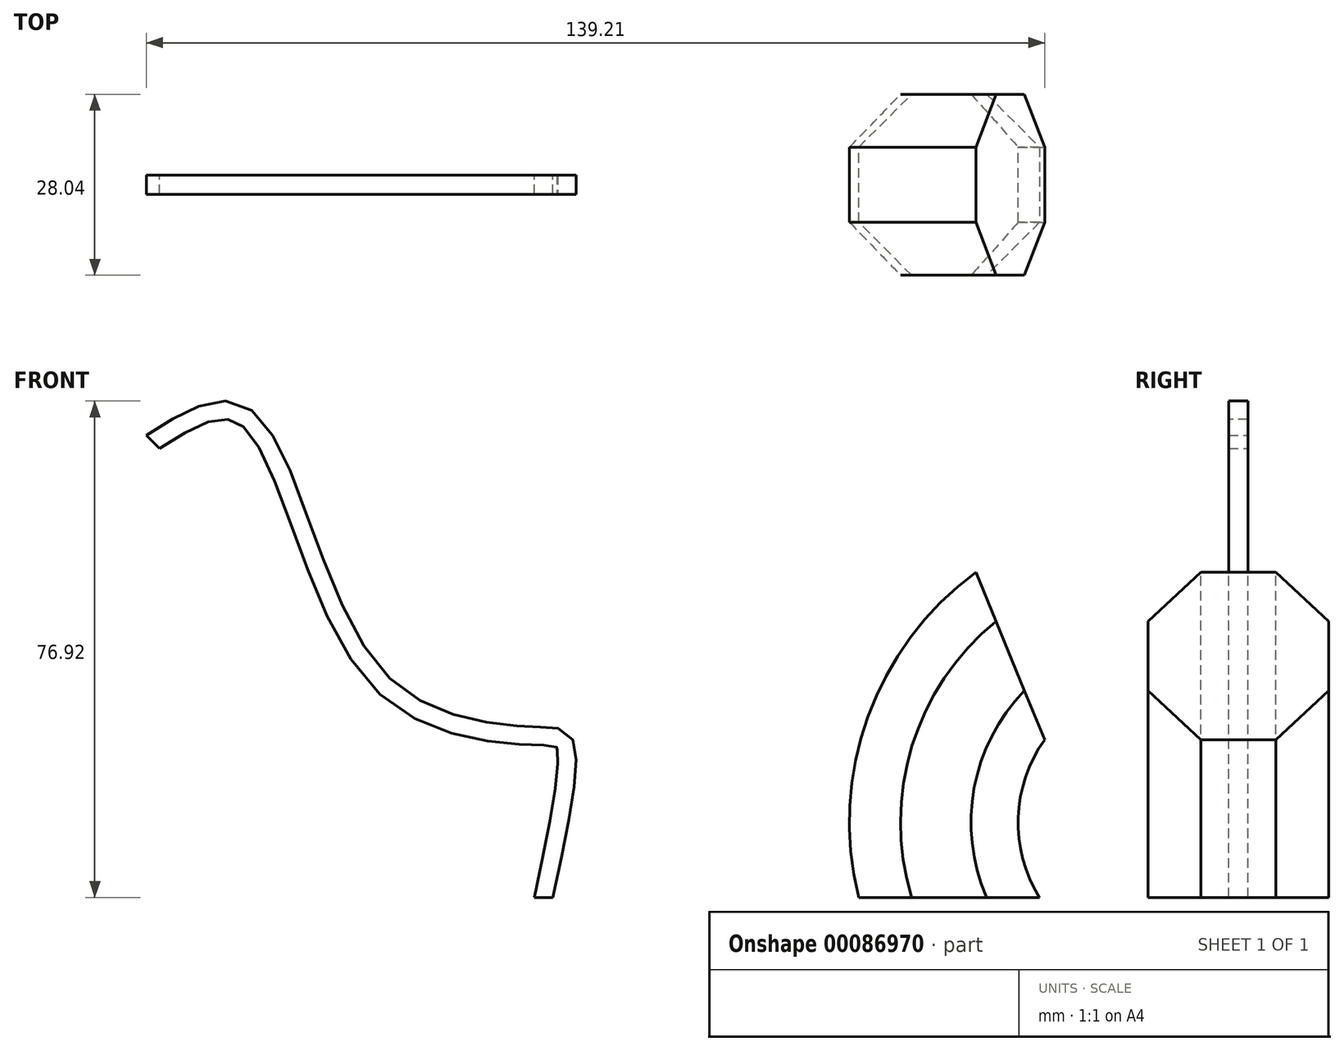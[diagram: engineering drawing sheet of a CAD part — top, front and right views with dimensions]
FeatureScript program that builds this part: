
annotation { "Feature Type Name" : "Feature", "Feature Type Description" : "" }
export const myFeature = defineFeature(function(context is Context, id is Id, definition is map)
    precondition{}
    {
        {
            var Q0;
            Q0=qCreatedBy(makeId("Front.planeOp"),FACE);
            var sketch = newSketch(context, id + "F0", { "sketchPlane" : qUnion([Q0])});
            skLineSegment(sketch, "E0", {"start": v(0, 0) * mm, "end": v(46.88, 0) * mm, "construction": true});
            skLineSegment(sketch, "E1", {"start": v(46.88, 0) * mm, "end": v(46.88, 46.88) * mm, "construction": true});
            skLineSegment(sketch, "E2", {"start": v(46.88, 46.88) * mm, "end": v(0, 0) * mm, "construction": true});
            skLineSegment(sketch, "E3", {"start": v(46.88, 0) * mm, "end": v(23.44, 23.44) * mm, "construction": true});
            skLineSegment(sketch, "E4", {"start": v(23.44, 23.44) * mm, "end": v(9.47, 37.41) * mm, "construction": true});
            skArc(sketch, "E5.trimOffspring", {"start": v(9.47, 37.41) * mm, "mid": v(-0.96, 20.15) * mm, "end": v(0, 0) * mm});
            skSolve(sketch);
        }
        {
            var Q0;
            Q0=qCreatedBy(makeId("Top.planeOp"),FACE);
            var sketch = newSketch(context, id + "F1", { "sketchPlane" : qUnion([Q0])});
            skCircle(sketch, "E6.cCircle", {"center": v(0, 0) * mm, "radius": 14.02 * mm, "construction": true});
            skLineSegment(sketch, "E6.0", {"start": v(5.8, -14.02) * mm, "end": v(-5.8, -14.02) * mm});
            skLineSegment(sketch, "E6.1", {"start": v(-5.8, -14.02) * mm, "end": v(-14.02, -5.8) * mm});
            skLineSegment(sketch, "E6.2", {"start": v(-14.02, -5.8) * mm, "end": v(-14.02, 5.8) * mm});
            skLineSegment(sketch, "E6.3", {"start": v(-14.02, 5.8) * mm, "end": v(-5.8, 14.02) * mm});
            skLineSegment(sketch, "E6.4", {"start": v(-5.8, 14.02) * mm, "end": v(5.8, 14.02) * mm});
            skLineSegment(sketch, "E6.5", {"start": v(5.8, 14.02) * mm, "end": v(14.02, 5.8) * mm});
            skLineSegment(sketch, "E6.6", {"start": v(14.02, 5.8) * mm, "end": v(14.02, -5.8) * mm});
            skLineSegment(sketch, "E6.7", {"start": v(14.02, -5.8) * mm, "end": v(5.8, -14.02) * mm});
            skPoint(sketch, "E6.0.midPoint", {"position": v(0, -14.02) * mm});
            skSolve(sketch);
        }
        {
            var Q0;
            Q0=makeQuery(id+"F1.imprint","IMPRINT",FACE,{"disambiguationData":[TD([[makeQuery(id+"F1.imprint","IMPRINT",EDGE,{"derivedFrom":sQuery(id+"F1.wireOp",EDGE,"E6.0")}),-1.0]])]});
            var Q1;
            Q1=sQuery(id+"F0.wireOp",EDGE,"E5.trimOffspring");
            sweep(context, id + "F2", {"profiles" : qUnion([Q0]), "path" : qUnion([Q1])});
        }
        {
            var Q0;
            Q0=qCreatedBy(makeId("Front.planeOp"),FACE);
            var sketch = newSketch(context, id + "F3", { "sketchPlane" : qUnion([Q0])});
            skFitSpline(sketch, "E7", {"points": [v(-62.87, 0) * mm, v(-59.54, 23.6) * mm, v(-62.68, 24.97) * mm, v(-88.14, 33.4) * mm, v(-108.9, 74.33) * mm, v(-123.4, 70.6) * mm], "startDerivative": vector(30.74, 142.34) * mm, "endDerivative": vector(-91.72, -58.96) * mm});
            skSolve(sketch);
        }
        {
            var Q0;
            Q0=qCreatedBy(makeId("Top.planeOp"),FACE);
            var sketch = newSketch(context, id + "F4", { "sketchPlane" : qUnion([Q0])});
            skLineSegment(sketch, "E8.bottom", {"start": v(-61.43, -1.5) * mm, "end": v(-64.32, -1.5) * mm});
            skLineSegment(sketch, "E8.top", {"start": v(-61.43, 1.5) * mm, "end": v(-64.32, 1.5) * mm});
            skLineSegment(sketch, "E8.left", {"start": v(-61.43, -1.5) * mm, "end": v(-61.43, 1.5) * mm});
            skLineSegment(sketch, "E8.right", {"start": v(-64.32, -1.5) * mm, "end": v(-64.32, 1.5) * mm});
            skPoint(sketch, "E8.middle", {"position": v(-62.87, 0) * mm});
            skSolve(sketch);
        }
        {
            var Q0;
            Q0=makeQuery(id+"F4.imprint","IMPRINT",FACE,{"disambiguationData":[TD([[makeQuery(id+"F4.imprint","IMPRINT",EDGE,{"derivedFrom":sQuery(id+"F4.wireOp",EDGE,"E8.bottom")}),-1.0]])]});
            var Q1;
            Q1=sQuery(id+"F3.wireOp",EDGE,"E7");
            sweep(context, id + "F5", {"profiles" : qUnion([Q0]), "path" : qUnion([Q1])});
        }
    });
